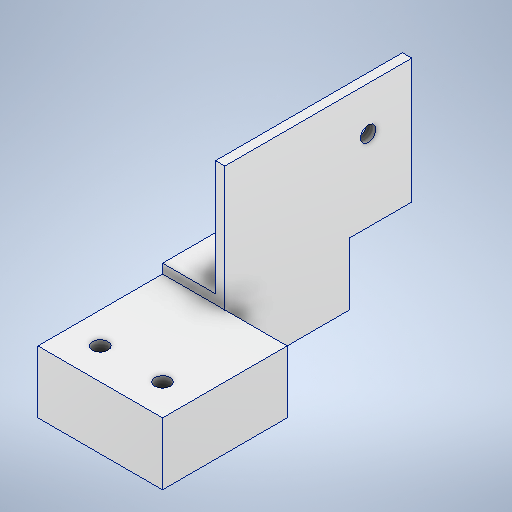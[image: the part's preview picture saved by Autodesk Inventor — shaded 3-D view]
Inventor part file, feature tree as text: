
AUTODESK INVENTOR PART (.ipt)
format: ipt  version: 2025 (Build 290162000, 162)  size: 284,672 bytes
history: native  units: mm
features: sketch x6, extrude x4, hole x2, projected_geometry x2, other x1
ambient origin geometry x8: Origin, YZ Plane, XZ Plane, XY Plane, X Axis, Y Axis, Z Axis, Center Point
bodies: Body1 (feature_tree)
feature tree (15):
  other  "Těleso1"
  extrude  "Vysunutí1"  Depth=20.0mm
  extrude  "Vysunutí2"  Depth=40.0mm
  hole  "Díra1"  [1 undecoded]
  extrude  "Vysunutí3"  TaperAngle=0.0deg  [1 undecoded]
  extrude  "Vysunutí4"  Depth=5.0mm
  hole  "Díra2"  [1 undecoded]
  sketch  "Náčrt1"
  sketch  "Náčrt2"
  projected_geometry  "Promítnutá smyčka1"
  sketch  "Náčrt3"
  sketch  "Náčrt4"
  sketch  "Náčrt5"
  sketch  "Náčrt6"
  projected_geometry  "Promítnutá smyčka2"
note: 3 required parameter values undecoded (feature->parameter linkage not recoverable at this tier; creation-order binding heuristic only, values carry confidence <= 0.55)
